# Revit family: ShowerTray-Vitra-VStoneSeries-5701813
name_source: partatom
category: Plumbing Fixtures
revit_build: Autodesk Revit 2017 (Build: 20160225_1515(x64)
units: mm (PartAtom-declared; Revit-internal decimal feet)

## family parameters
Cut with Voids When Loaded = No
Host = Face
OmniClass Number = 23.45.05.14.17
OmniClass Title = Showers
Part Type = Normal
Room Calculation Point = No
Round Connector Dimension = Use Diameter
Shared = Yes

## types (18) — shared parameters
BIMobject category = Sanitary - Shower trays
CW Connection = No
Description = VitrA V-Stone Shower Tray
Design country = Turkey
HW Connection = No
IFC Classification = Sanitary Terminal
Installation instructions = https://cdn.vitra.com.tr
Main Material = Ceramic
Manufacturer = Vitra
Manufacturer name = Vitra
Masterformat 2014 Code = 22 41 23
Masterformat 2014 Description = Residential Showers
MountingType = Floor Mounted
NBS Referans Code = 35-06-84
NBS Referans Description = Shower Trays
NominalHeight = 35 mm  [stored 0.114829 ft]
OmniClass Code = 23-31 17 00
OmniClass Description = Showers
Product Guid = https://cdn.vitra.com.tr
Product certification = https://vitraglobal.com
Product data url = https://www.vitraglobal.com
Product family = Floor Mounted Shower Tray
Product group = V-Stone
Technical description = https://www.vitraglobal.com
UNSPSC Code = 301815
URL = https://vitraglobal.com
Uniclass 1.4 Code = L7214
Uniclass 1.4 Description = Showers
Uniclass 2.0 Code = PR-35-06-84
Uniclass 2.0 Description = Shower Trays
Uniclass 2015 Code = Pr_40_20_06_84
Uniclass 2015 Name = Shower trays
Uniformat II Code = D2010
Uniformat II Description = Plumbing Fixtures
Vent Connection = No
Warranty Period (Year) = 10 Years
Waste Connection = Yes
Youtube = https://www.youtube.com
zero-valued in all types: Cost, Default Elevation

## per-type parameters (varying)
| type | Article No. (default) | Color | Model | Nominal Depth | NominalWidth | Product SKU | Secondary Material | Weight Net (kg) |
| ShowerTray-Solidstone-Vitra-VStoneSeries(90x90)(White)_5701813 | 5701813 | White | 5701813 | 900 mm  [stored 2.95276 ft] | 900 mm  [stored 2.95276 ft] | 5701813 | Ceramic-White | 45,000 |
| ShowerTray-Solidstone-Vitra-VStoneSeries(100x80)(White)_5701814 | 5701814 | White | 5701814 | 1000 mm  [stored 3.28084 ft] | 800 mm  [stored 2.62467 ft] | 5701814 | Ceramic-White | 45,000 |
| ShowerTray-Solidstone-Vitra-VStoneSeries(120x80)(White)_5701815 | 5701815 | White | 5701815 | 1200 mm | 800 mm  [stored 2.62467 ft] | 5701815 | Ceramic-White | 53,000 |
| ShowerTray-Solidstone-Vitra-VStoneSeries(140x80)(White)_5701816 | 5701816 | White | 5701816 | 1400 mm  [stored 4.59318 ft] | 800 mm  [stored 2.62467 ft] | 5701816 | Ceramic-White | 62,000 |
| ShowerTray-Solidstone-Vitra-VStoneSeries(120x90)(White)_5701817 | 5701817 | White | 5701817 | 1200 mm | 900 mm  [stored 2.95276 ft] | 5701817 | Ceramic-White | 60,000 |
| ShowerTray-Solidstone-Vitra-VStoneSeries(140x90)(White)_5701818 | 5701818 | White | 5701818 | 1400 mm  [stored 4.59318 ft] | 900 mm  [stored 2.95276 ft] | 5701818 | Ceramic-White | 69,000 |
| ShowerTray-Solidstone-Vitra-VStoneSeries(90x90)(Gray)_5701819 | 5701819 | Gray | 5701819 | 900 mm  [stored 2.95276 ft] | 900 mm  [stored 2.95276 ft] | 5701819 | Gray | 45,000 |
| ShowerTray-Solidstone-Vitra-VStoneSeries(100x80)(Gray)_5701850 | 5701850 | Gray | 5701850 | 1000 mm  [stored 3.28084 ft] | 800 mm  [stored 2.62467 ft] | 5701850 | Gray | 45,000 |
| ShowerTray-Solidstone-Vitra-VStoneSeries(120x80)(Gray)_5701851 | 5701851 | Gray | 5701851 | 1200 mm | 800 mm  [stored 2.62467 ft] | 5701851 | Gray | 53,000 |
| ShowerTray-Solidstone-Vitra-VStoneSeries(140x80)(Gray)_5701852 | 5701852 | Gray | 5701852 | 1400 mm  [stored 4.59318 ft] | 800 mm  [stored 2.62467 ft] | 5701852 | Gray | 62,000 |
| ShowerTray-Solidstone-Vitra-VStoneSeries(120x90)(Gray)_5701853 | 5701853 | Gray | 5701853 | 1200 mm | 900 mm  [stored 2.95276 ft] | 5701853 | Gray | 60,000 |
| ShowerTray-Solidstone-Vitra-VStoneSeries(140x90)(Gray)_5701854 | 5701854 | Gray | 5701854 | 1400 mm  [stored 4.59318 ft] | 900 mm  [stored 2.95276 ft] | 5701854 | Gray | 69,000 |
| ShowerTray-Solidstone-Vitra-VStoneSeries(90x90)(Antrasit)_5701855 | 5701855 | Antrasit | 5701855 | 900 mm  [stored 2.95276 ft] | 900 mm  [stored 2.95276 ft] | 5701855 | Antrasit | 45,000 |
| ShowerTray-Solidstone-Vitra-VStoneSeries(100x80)(Antrasit)_5701856 | 5701856 | Antrasit | 5701856 | 1000 mm  [stored 3.28084 ft] | 800 mm  [stored 2.62467 ft] | 5701856 | Antrasit | 45,000 |
| ShowerTray-Solidstone-Vitra-VStoneSeries(120x80)(Antrasit)_5701857 | 5701857 | Antrasit | 5701857 | 1200 mm | 800 mm  [stored 2.62467 ft] | 5701857 | Antrasit | 53,000 |
| ShowerTray-Solidstone-Vitra-VStoneSeries(140x80)(Antrasit)_5701858 | 5701858 | Antrasit | 5701858 | 1400 mm  [stored 4.59318 ft] | 800 mm  [stored 2.62467 ft] | 5701858 | Antrasit | 62,000 |
| ShowerTray-Solidstone-Vitra-VStoneSeries(120x90)(Antrasit)_5701859 | 5701859 | Antrasit | 5701859 | 1200 mm | 900 mm  [stored 2.95276 ft] | 5701859 | Antrasit | 60,000 |
| ShowerTray-Solidstone-Vitra-VStoneSeries(140x90)(Antrasit)_5701860 | 5701860 | Antrasit | 5701860 | 1400 mm  [stored 4.59318 ft] | 900 mm  [stored 2.95276 ft] | 5701860 | Antrasit | 69,000 |

note: [stored X ft] marks values corroborated as IEEE doubles in the binary element streams (Revit-internal decimal feet)

## geometry (parser evidence)
native form markers: Sweep x3
no freeform markers — native parametric forms only
